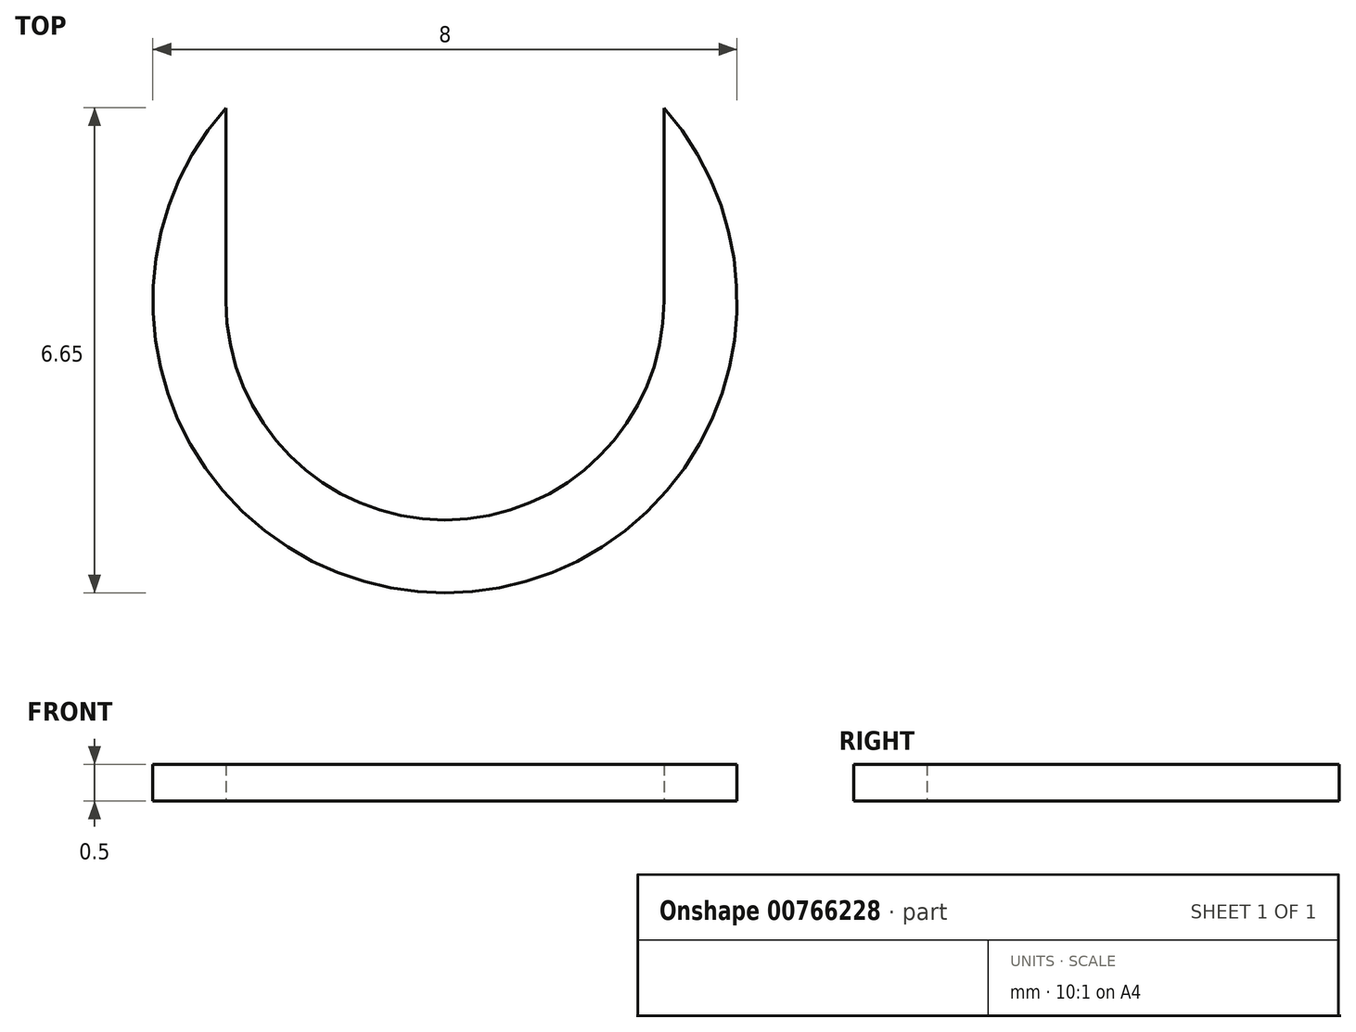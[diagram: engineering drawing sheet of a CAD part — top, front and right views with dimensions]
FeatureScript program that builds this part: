
annotation { "Feature Type Name" : "Feature", "Feature Type Description" : "" }
export const myFeature = defineFeature(function(context is Context, id is Id, definition is map)
    precondition{}
    {
        {
            var Q0;
            Q0=qCreatedBy(makeId("Top.planeOp"),FACE);
            var sketch = newSketch(context, id + "F0", { "sketchPlane" : qUnion([Q0])});
            skCircle(sketch, "E0", {"center": v(0, 0) * mm, "radius": 3 * mm});
            skCircle(sketch, "E1", {"center": v(0, 0) * mm, "radius": 4 * mm});
            skLineSegment(sketch, "E2", {"start": v(-3, 0) * mm, "end": v(-3, 5.41) * mm});
            skLineSegment(sketch, "E3", {"start": v(3, 0) * mm, "end": v(3, 5.34) * mm});
            skSolve(sketch);
        }
        {
            var Q0;
            {var subQ0=sQuery(id+"F0.wireOp",EDGE,"E2");var subQ1=sQuery(id+"F0.wireOp",EDGE,"E0");var subQ2=makeQuery(id+"F0.imprint","INTERSECT",VERTEX,{"derivedFrom":[subQ1,subQ0]});Q0=makeQuery(id+"F0.imprint","IMPRINT",FACE,{"disambiguationData":[TD([[makeQuery(id+"F0.imprint","IMPRINT",EDGE,{"disambiguationData":[TD([[subQ2,-1.0]])],"derivedFrom":subQ1}),-1.0]])]});}
            extrude(context, id + "F1", {"entities" : qUnion([Q0]), "depth" : 0.5 * mm, "offsetDistance" : 25 * mm});
        }
    });
